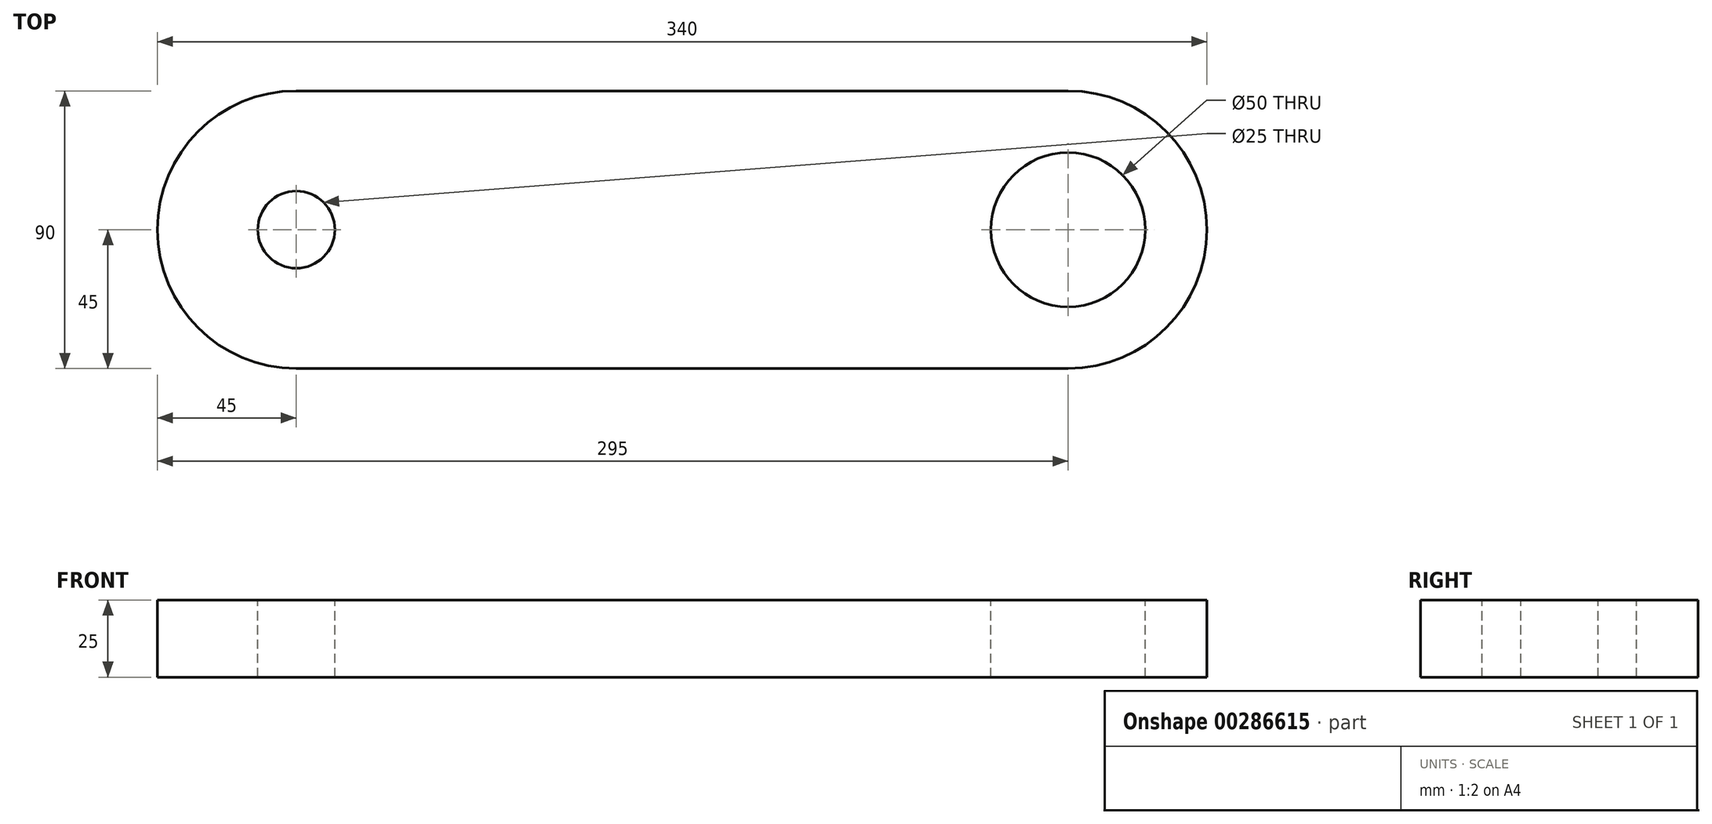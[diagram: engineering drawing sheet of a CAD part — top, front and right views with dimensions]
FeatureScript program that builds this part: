
annotation { "Feature Type Name" : "Feature", "Feature Type Description" : "" }
export const myFeature = defineFeature(function(context is Context, id is Id, definition is map)
    precondition{}
    {
        {
            var Q0;
            Q0=qCreatedBy(makeId("Top.planeOp"),FACE);
            var sketch = newSketch(context, id + "F0", { "sketchPlane" : qUnion([Q0])});
            skArc(sketch, "E0", {"start": v(0, 45) * mm, "mid": v(-45, 0) * mm, "end": v(0, -45) * mm});
            skArc(sketch, "E1", {"start": v(250, -45) * mm, "mid": v(295, 0) * mm, "end": v(250, 45) * mm});
            skLineSegment(sketch, "E2", {"start": v(0, 45) * mm, "end": v(250, 45) * mm});
            skLineSegment(sketch, "E3", {"start": v(0, -45) * mm, "end": v(250, -45) * mm});
            skSolve(sketch);
        }
        {
            var Q0;
            Q0=makeQuery(id+"F0.imprint","IMPRINT",FACE,{"disambiguationData":[TD([[makeQuery(id+"F0.imprint","IMPRINT",EDGE,{"derivedFrom":sQuery(id+"F0.wireOp",EDGE,"E0")}),1.0]])]});
            extrude(context, id + "F1", {"entities" : qUnion([Q0]), "depth" : 25 * mm});
        }
        {
            var Q0;
            Q0=makeQuery(id+"F1.opExtrude","CAP_FACE",FACE,{"disambiguationData":[OSD([sQuery(id+"F0.wireOp",EDGE,"E0"),sQuery(id+"F0.wireOp",EDGE,"E1"),sQuery(id+"F0.wireOp",EDGE,"E2"),sQuery(id+"F0.wireOp",EDGE,"E3")])],"isStart":false});
            var sketch = newSketch(context, id + "F2", { "sketchPlane" : qUnion([Q0])});
            skCircle(sketch, "E4", {"center": v(0, 0) * mm, "radius": 12.5 * mm});
            skCircle(sketch, "E5", {"center": v(250, 0) * mm, "radius": 25 * mm});
            skSolve(sketch);
        }
        {
            var Q0;
            Q0=makeQuery(id+"F2.imprint","IMPRINT",FACE,{"disambiguationData":[TD([[makeQuery(id+"F2.imprint","IMPRINT",EDGE,{"derivedFrom":sQuery(id+"F2.wireOp",EDGE,"E4")}),1.0]])]});
            var Q1;
            Q1=makeQuery(id+"F2.imprint","IMPRINT",FACE,{"disambiguationData":[TD([[makeQuery(id+"F2.imprint","IMPRINT",EDGE,{"derivedFrom":sQuery(id+"F2.wireOp",EDGE,"E5")}),1.0]])]});
            extrude(context, id + "F3", {"entities" : qUnion([Q0, Q1]), "operationType" : NewBodyOperationType.REMOVE, "endBound" : BoundingType.THROUGH_ALL, "oppositeDirection" : true, "depth" : 25 * mm});
        }
    });
